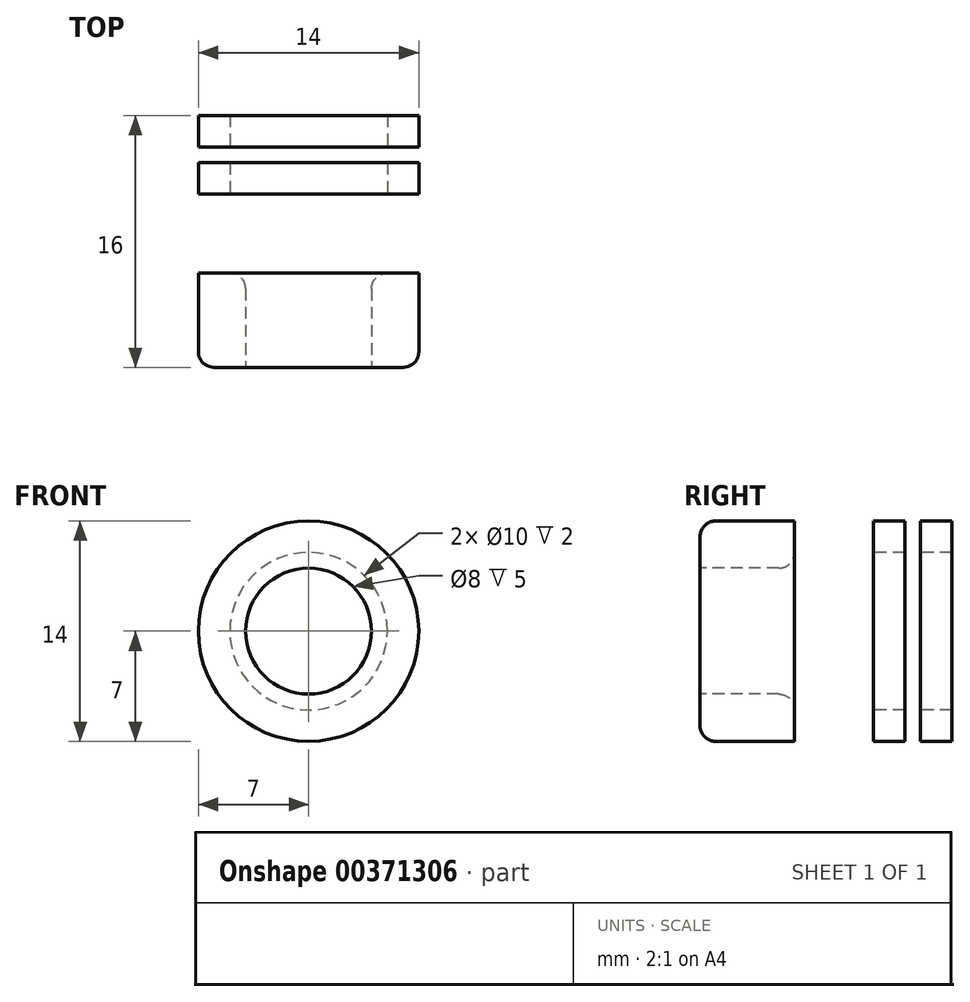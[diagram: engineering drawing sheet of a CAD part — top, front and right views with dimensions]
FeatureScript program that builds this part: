
annotation { "Feature Type Name" : "Feature", "Feature Type Description" : "" }
export const myFeature = defineFeature(function(context is Context, id is Id, definition is map)
    precondition{}
    {
        {
            var Q0;
            Q0=qCreatedBy(makeId("Top.planeOp"),FACE);
            var sketch = newSketch(context, id + "F0", { "sketchPlane" : qUnion([Q0])});
            skLineSegment(sketch, "E0.bottom", {"start": v(36, -27.53) * mm, "end": v(38, -27.53) * mm});
            skLineSegment(sketch, "E0.top", {"start": v(37, -21.53) * mm, "end": v(39, -21.53) * mm});
            skLineSegment(sketch, "E0.left", {"start": v(36, -27.53) * mm, "end": v(36, -22.53) * mm});
            skLineSegment(sketch, "E0.right", {"start": v(39, -26.53) * mm, "end": v(39, -21.53) * mm});
            skLineSegment(sketch, "E1.bottom", {"start": v(39, -21.53) * mm, "end": v(37, -21.53) * mm});
            skLineSegment(sketch, "E1.top", {"start": v(39, -19.53) * mm, "end": v(37, -19.53) * mm});
            skLineSegment(sketch, "E1.left", {"start": v(39, -21.53) * mm, "end": v(39, -19.53) * mm});
            skLineSegment(sketch, "E1.right", {"start": v(37, -21.53) * mm, "end": v(37, -19.53) * mm});
            skLineSegment(sketch, "E2.bottom", {"start": v(37, -19.53) * mm, "end": v(38, -19.53) * mm});
            skLineSegment(sketch, "E2.top", {"start": v(37, -18.53) * mm, "end": v(38, -18.53) * mm});
            skLineSegment(sketch, "E2.left", {"start": v(37, -19.53) * mm, "end": v(37, -18.53) * mm});
            skLineSegment(sketch, "E2.right", {"start": v(38, -19.53) * mm, "end": v(38, -18.53) * mm});
            skLineSegment(sketch, "E3.bottom", {"start": v(37, -18.53) * mm, "end": v(39, -18.53) * mm});
            skLineSegment(sketch, "E3.top", {"start": v(37, -16.53) * mm, "end": v(39, -16.53) * mm});
            skLineSegment(sketch, "E3.left", {"start": v(37, -18.53) * mm, "end": v(37, -16.53) * mm});
            skLineSegment(sketch, "E3.right", {"start": v(39, -18.53) * mm, "end": v(39, -16.53) * mm});
            skPoint(sketch, "E4.oppositeSnap0", {"position": v(38, -16.53) * mm});
            skLineSegment(sketch, "E4.bottom", {"start": v(37, -16.53) * mm, "end": v(38, -16.53) * mm});
            skLineSegment(sketch, "E4.top", {"start": v(37, -15.53) * mm, "end": v(38, -15.53) * mm});
            skLineSegment(sketch, "E4.left", {"start": v(37, -16.53) * mm, "end": v(37, -15.53) * mm});
            skLineSegment(sketch, "E4.right", {"start": v(38, -16.53) * mm, "end": v(38, -15.53) * mm});
            skLineSegment(sketch, "E5.bottom", {"start": v(37, -15.53) * mm, "end": v(39, -15.53) * mm});
            skLineSegment(sketch, "E5.top", {"start": v(37, -13.53) * mm, "end": v(39, -13.53) * mm});
            skLineSegment(sketch, "E5.left", {"start": v(37, -15.53) * mm, "end": v(37, -13.53) * mm});
            skLineSegment(sketch, "E5.right", {"start": v(39, -15.53) * mm, "end": v(39, -13.53) * mm});
            skLineSegment(sketch, "E6.bottom", {"start": v(39, -13.53) * mm, "end": v(37, -13.53) * mm});
            skLineSegment(sketch, "E6.top", {"start": v(38, -7.53) * mm, "end": v(37, -7.53) * mm});
            skLineSegment(sketch, "E6.left", {"start": v(39, -13.53) * mm, "end": v(39, -8.53) * mm});
            skLineSegment(sketch, "E6.right", {"start": v(36, -12.53) * mm, "end": v(36, -8.53) * mm});
            skLineSegment(sketch, "E7", {"start": v(32, -27.53) * mm, "end": v(32, -7.53) * mm});
            skPoint(sketch, "E8.visualSharp", {"position": v(36, -21.53) * mm});
            skArc(sketch, "E8.filletArc", {"start": v(37, -21.53) * mm, "mid": v(36.3, -21.82) * mm, "end": v(36, -22.53) * mm});
            skPoint(sketch, "E9.visualSharp", {"position": v(39, -27.53) * mm});
            skArc(sketch, "E9.filletArc", {"start": v(38, -27.53) * mm, "mid": v(38.7, -27.23) * mm, "end": v(39, -26.53) * mm});
            skPoint(sketch, "E10.visualSharp", {"position": v(39, -7.53) * mm});
            skArc(sketch, "E10.filletArc", {"start": v(39, -8.53) * mm, "mid": v(38.7, -7.82) * mm, "end": v(38, -7.53) * mm});
            skPoint(sketch, "E11.visualSharp", {"position": v(36, -7.53) * mm});
            skArc(sketch, "E11.filletArc", {"start": v(37, -7.53) * mm, "mid": v(36.3, -7.82) * mm, "end": v(36, -8.53) * mm});
            skPoint(sketch, "E12.visualSharp", {"position": v(36, -13.53) * mm});
            skArc(sketch, "E12.filletArc", {"start": v(36, -12.53) * mm, "mid": v(36.3, -13.23) * mm, "end": v(37, -13.53) * mm});
            skSolve(sketch);
        }
        {
            var Q0;
            Q0=makeQuery(id+"F0.imprint","IMPRINT",FACE,{"disambiguationData":[TD([[makeQuery(id+"F0.imprint","IMPRINT",EDGE,{"derivedFrom":sQuery(id+"F0.wireOp",EDGE,"E0.bottom")}),1.0]])]});
            var Q1;
            Q1=makeQuery(id+"F0.imprint","IMPRINT",FACE,{"disambiguationData":[TD([[makeQuery(id+"F0.imprint","IMPRINT",EDGE,{"derivedFrom":sQuery(id+"F0.wireOp",EDGE,"E1.bottom")}),-1.0]])]});
            var Q2;
            Q2=makeQuery(id+"F0.imprint","IMPRINT",FACE,{"disambiguationData":[TD([[makeQuery(id+"F0.imprint","IMPRINT",EDGE,{"derivedFrom":sQuery(id+"F0.wireOp",EDGE,"E2.bottom")}),1.0]])]});
            var Q3;
            Q3=makeQuery(id+"F0.imprint","IMPRINT",FACE,{"disambiguationData":[TD([[makeQuery(id+"F0.imprint","IMPRINT",EDGE,{"derivedFrom":sQuery(id+"F0.wireOp",EDGE,"E3.top")}),-1.0]])]});
            var Q4;
            Q4=makeQuery(id+"F0.imprint","IMPRINT",FACE,{"disambiguationData":[TD([[makeQuery(id+"F0.imprint","IMPRINT",EDGE,{"derivedFrom":sQuery(id+"F0.wireOp",EDGE,"E4.bottom")}),1.0]])]});
            var Q5;
            {var subQ1=sQuery(id+"F0.wireOp",EDGE,"E5.left");Q5=makeQuery(id+"F0.imprint","IMPRINT",FACE,{"disambiguationData":[TD([[makeQuery(id+"F0.imprint","IMPRINT",EDGE,{"derivedFrom":subQ1}),-1.0]])]});}
            var Q6;
            Q6=makeQuery(id+"F0.imprint","IMPRINT",FACE,{"disambiguationData":[TD([[makeQuery(id+"F0.imprint","IMPRINT",EDGE,{"derivedFrom":sQuery(id+"F0.wireOp",EDGE,"E6.bottom")}),-1.0]])]});
            var Q7;
            Q7=sQuery(id+"F0.wireOp",EDGE,"E7");
            revolve(context, id + "F1", {"entities" : qUnion([Q0, Q1, Q2, Q3, Q4, Q5, Q6]), "axis" : qUnion([Q7]), "revolveType" : RevolveType.FULL});
        }
        {
            var Q0;
            Q0=makeQuery(id+"F1.opRevolve","SWEPT_BODY",BODY,{"disambiguationData":[OSD([sQuery(id+"F0.wireOp",EDGE,"E0.bottom"),sQuery(id+"F0.wireOp",EDGE,"E0.left"),sQuery(id+"F0.wireOp",EDGE,"E0.right"),sQuery(id+"F0.wireOp",EDGE,"E1.top"),sQuery(id+"F0.wireOp",EDGE,"E1.left"),sQuery(id+"F0.wireOp",EDGE,"E1.right"),sQuery(id+"F0.wireOp",EDGE,"E2.left"),sQuery(id+"F0.wireOp",EDGE,"E2.right"),sQuery(id+"F0.wireOp",EDGE,"E3.bottom"),sQuery(id+"F0.wireOp",EDGE,"E3.top"),sQuery(id+"F0.wireOp",EDGE,"E3.left"),sQuery(id+"F0.wireOp",EDGE,"E3.right"),sQuery(id+"F0.wireOp",EDGE,"E4.left"),sQuery(id+"F0.wireOp",EDGE,"E4.right"),sQuery(id+"F0.wireOp",EDGE,"E5.bottom"),sQuery(id+"F0.wireOp",EDGE,"E5.left"),sQuery(id+"F0.wireOp",EDGE,"E5.right"),sQuery(id+"F0.wireOp",EDGE,"E6.top"),sQuery(id+"F0.wireOp",EDGE,"E6.left"),sQuery(id+"F0.wireOp",EDGE,"E6.right"),sQuery(id+"F0.wireOp",EDGE,"E8.filletArc"),sQuery(id+"F0.wireOp",EDGE,"E9.filletArc"),sQuery(id+"F0.wireOp",EDGE,"E10.filletArc"),sQuery(id+"F0.wireOp",EDGE,"E11.filletArc"),sQuery(id+"F0.wireOp",EDGE,"E12.filletArc")])]});
            transform(context, id + "F2", {"entities" : qUnion([Q0]), "transformType" : TransformType.TRANSLATION_3D, "dx" : 0 * mm, "dy" : -2 * mm, "dz" : 0 * mm, "makeCopy" : false});
        }
    });
